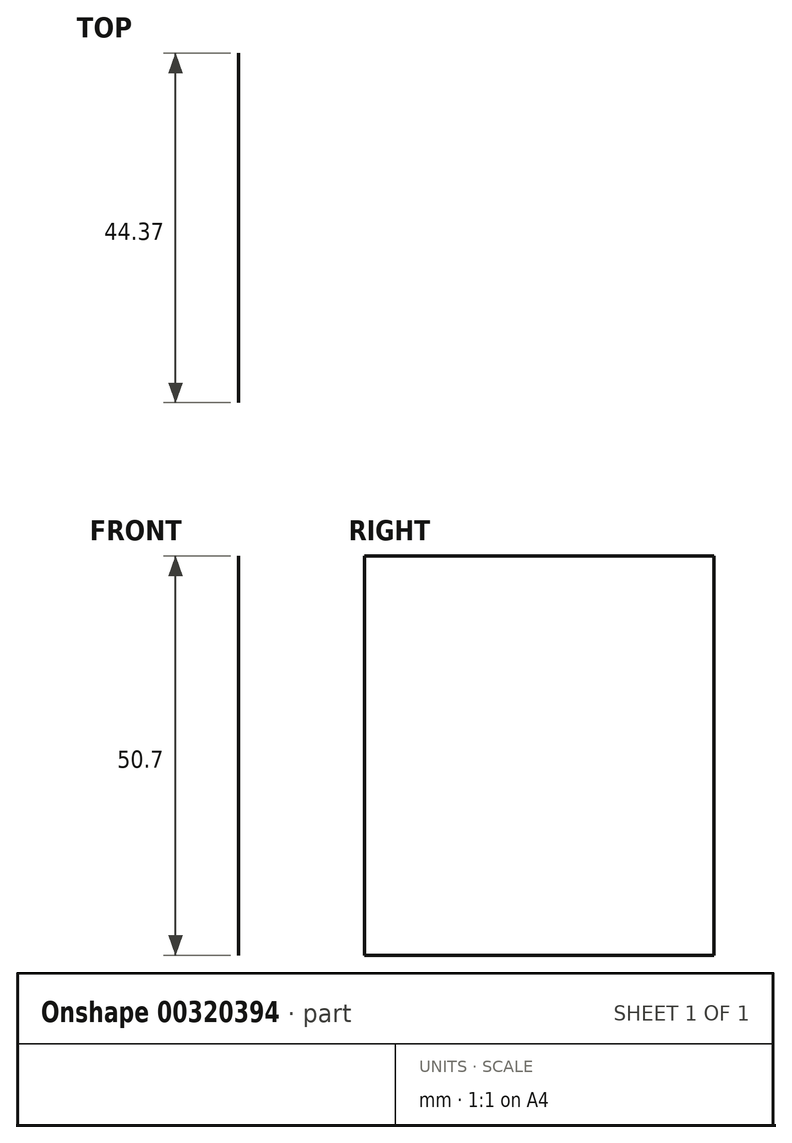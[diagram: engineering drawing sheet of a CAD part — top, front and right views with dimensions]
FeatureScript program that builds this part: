
annotation { "Feature Type Name" : "Feature", "Feature Type Description" : "" }
export const myFeature = defineFeature(function(context is Context, id is Id, definition is map)
    precondition{}
    {
        {
            var Q0;
            Q0=qCreatedBy(makeId("Top.planeOp"),FACE);
            var sketch = newSketch(context, id + "F0", { "sketchPlane" : qUnion([Q0])});
            skLineSegment(sketch, "E0.bottom", {"start": v(0, 44.37) * mm, "end": v(0, 44.37) * mm});
            skLineSegment(sketch, "E0.top", {"start": v(0, 36.82) * mm, "end": v(0, 36.82) * mm});
            skLineSegment(sketch, "E0.left", {"start": v(0, 44.37) * mm, "end": v(0, 36.82) * mm});
            skLineSegment(sketch, "E0.right", {"start": v(0, 44.37) * mm, "end": v(0, 36.82) * mm});
            skLineSegment(sketch, "E1.bottom", {"start": v(17.64, 44.37) * mm, "end": v(43.51, 44.37) * mm});
            skLineSegment(sketch, "E1.top", {"start": v(17.64, 0) * mm, "end": v(43.51, 0) * mm});
            skLineSegment(sketch, "E1.left", {"start": v(17.64, 44.37) * mm, "end": v(17.64, 0) * mm});
            skLineSegment(sketch, "E1.right", {"start": v(43.51, 44.37) * mm, "end": v(43.51, 0) * mm});
            skSolve(sketch);
        }
        {
            var Q0;
            Q0 = qSketchRegion(id + "F0", true);
            var Q1;
            Q1=sQuery(id+"F0.wireOp",EDGE,"E1.left");
            extrude(context, id + "F1", {"entities" : qUnion([Q0]), "bodyType" : ToolBodyType.SURFACE, "surfaceEntities" : qUnion([Q1]), "depth" : 50.7 * mm});
        }
    });
